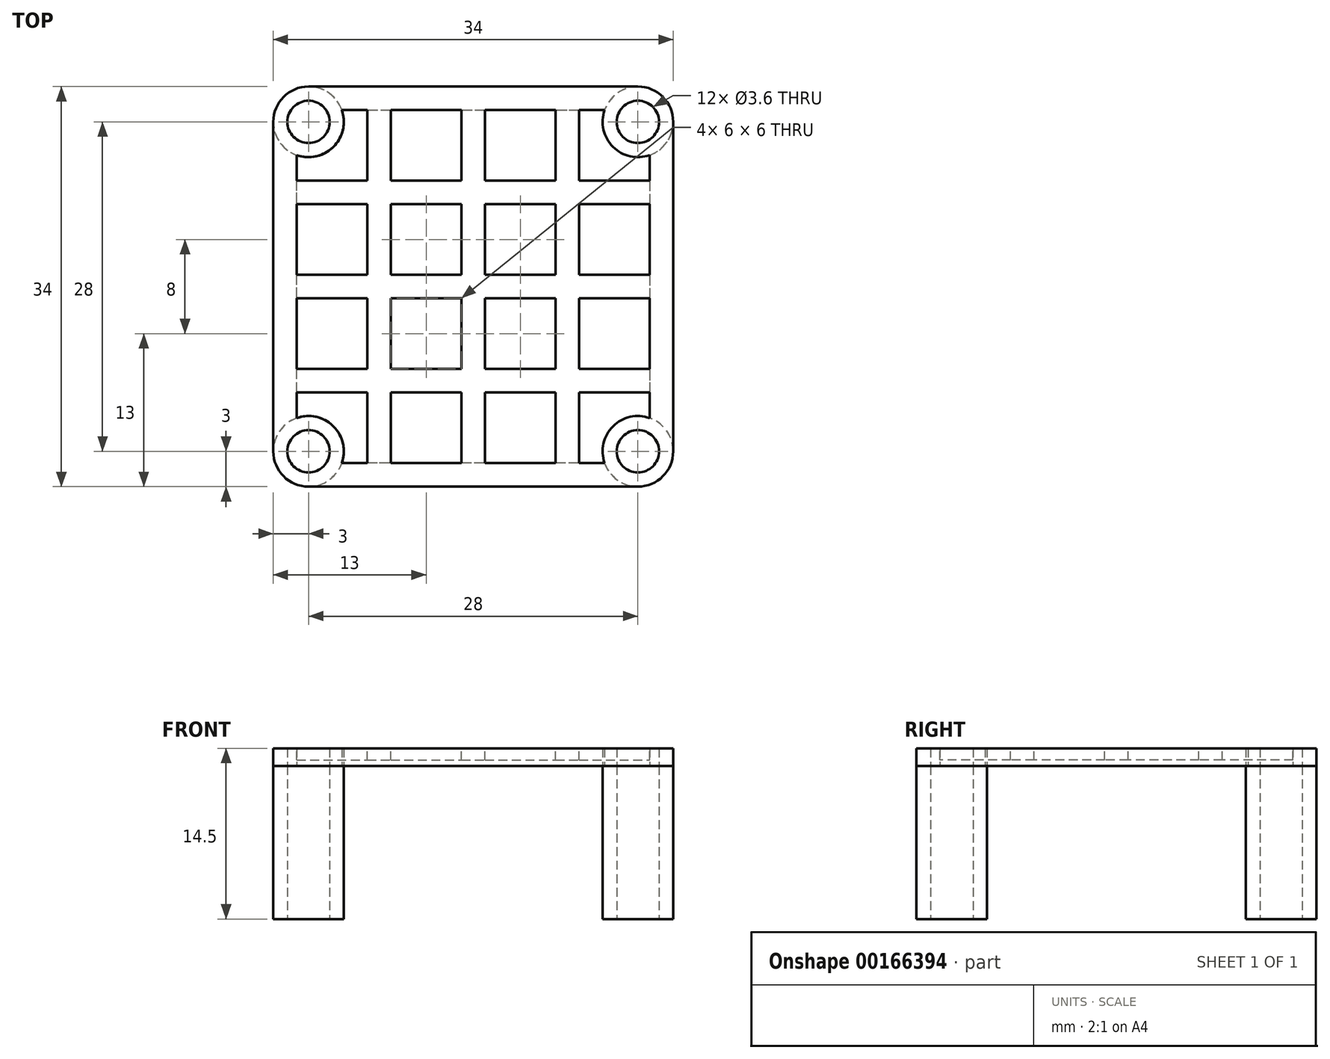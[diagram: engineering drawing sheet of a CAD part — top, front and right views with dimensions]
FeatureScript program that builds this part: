
annotation { "Feature Type Name" : "Feature", "Feature Type Description" : "" }
export const myFeature = defineFeature(function(context is Context, id is Id, definition is map)
    precondition{}
    {
        {
            var Q0;
            Q0=qCreatedBy(makeId("Top.planeOp"),FACE);
            var sketch = newSketch(context, id + "F0", { "sketchPlane" : qUnion([Q0])});
            skCircle(sketch, "E0", {"center": v(14, 14) * mm, "radius": 1.8 * mm});
            skCircle(sketch, "E1", {"center": v(-14, 14) * mm, "radius": 1.8 * mm});
            skCircle(sketch, "E2", {"center": v(-14, -14) * mm, "radius": 1.8 * mm});
            skCircle(sketch, "E3", {"center": v(14, -14) * mm, "radius": 1.8 * mm});
            skCircle(sketch, "E4", {"center": v(-14, 14) * mm, "radius": 3 * mm});
            skCircle(sketch, "E5", {"center": v(-14, -14) * mm, "radius": 3 * mm});
            skCircle(sketch, "E6", {"center": v(14, -14) * mm, "radius": 3 * mm});
            skCircle(sketch, "E7", {"center": v(14, 14) * mm, "radius": 3 * mm});
            skLineSegment(sketch, "E8", {"start": v(17, 14) * mm, "end": v(17, -14) * mm});
            skSolve(sketch);
        }
        {
            var Q0;
            Q0 = qSketchRegion(id + "F0", true);
            extrude(context, id + "F1", {"entities" : qUnion([Q0]), "depth" : 13 * mm});
        }
        {
            var Q0;
            Q0=makeQuery(id+"F1.opExtrude","CAP_FACE",FACE,{"disambiguationData":[OSD([sQuery(id+"F0.wireOp",EDGE,"E0"),sQuery(id+"F0.wireOp",EDGE,"E1"),sQuery(id+"F0.wireOp",EDGE,"E2"),sQuery(id+"F0.wireOp",EDGE,"E3"),sQuery(id+"F0.wireOp",EDGE,"E4"),sQuery(id+"F0.wireOp",EDGE,"E5"),sQuery(id+"F0.wireOp",EDGE,"E6"),sQuery(id+"F0.wireOp",EDGE,"E7"),sQuery(id+"F0.wireOp",EDGE,"E8"),sQuery(id+"F0.wireOp",EDGE,"9i3S1Yhi-saMO-If9d-kcrl-0AW5lP11ECcG"),sQuery(id+"F0.wireOp",EDGE,"0W7b4J66-iXpZ-pcOm-YQU5-B3qUaQrYBzQB"),sQuery(id+"F0.wireOp",EDGE,"YHf7HNGq-JsbW-y9zw-wNTN-EviQUekIIshC")])],"isStart":false});
            var sketch = newSketch(context, id + "F2", { "sketchPlane" : qUnion([Q0])});
            skArc(sketch, "E9.0", {"start": v(-15, 11.17) * mm, "mid": v(-11.88, 11.88) * mm, "end": v(-11.17, 15) * mm});
            skCircle(sketch, "E9.1", {"center": v(-14, 14) * mm, "radius": 1.8 * mm});
            skArc(sketch, "E9.2", {"start": v(11.17, 15) * mm, "mid": v(11.88, 11.88) * mm, "end": v(15, 11.17) * mm});
            skCircle(sketch, "E9.3", {"center": v(14, 14) * mm, "radius": 1.8 * mm});
            skArc(sketch, "E9.4", {"start": v(15, -11.17) * mm, "mid": v(11.88, -11.88) * mm, "end": v(11.17, -15) * mm});
            skCircle(sketch, "E9.5", {"center": v(14, -14) * mm, "radius": 1.8 * mm});
            skCircle(sketch, "E9.6", {"center": v(-14, -14) * mm, "radius": 1.8 * mm});
            skArc(sketch, "E9.7", {"start": v(-11.17, -15) * mm, "mid": v(-11.88, -11.88) * mm, "end": v(-15, -11.17) * mm});
            skLineSegment(sketch, "E10", {"start": v(-14, 17) * mm, "end": v(14, 17) * mm});
            skLineSegment(sketch, "E11", {"start": v(17, 14) * mm, "end": v(17, -14) * mm});
            skLineSegment(sketch, "E12", {"start": v(14, -17) * mm, "end": v(-14, -17) * mm});
            skLineSegment(sketch, "E13", {"start": v(-17, -14) * mm, "end": v(-17, 14) * mm});
            skLineSegment(sketch, "E14.0", {"start": v(-15, -11.17) * mm, "end": v(-15, 11.17) * mm});
            skLineSegment(sketch, "E15.trimOffspring", {"start": v(-11.17, 15) * mm, "end": v(11.17, 15) * mm});
            skArc(sketch, "E16.trimOffspring", {"start": v(-14, 17) * mm, "mid": v(-16.12, 16.12) * mm, "end": v(-17, 14) * mm});
            skArc(sketch, "E17.trimOffspring", {"start": v(17, 14) * mm, "mid": v(16.12, 16.12) * mm, "end": v(14, 17) * mm});
            skLineSegment(sketch, "E18.trimOffspring", {"start": v(15, 11.17) * mm, "end": v(15, -11.17) * mm});
            skLineSegment(sketch, "E19.trimOffspring", {"start": v(11.17, -15) * mm, "end": v(-11.17, -15) * mm});
            skArc(sketch, "E20.trimOffspring", {"start": v(14, -17) * mm, "mid": v(16.12, -16.12) * mm, "end": v(17, -14) * mm});
            skArc(sketch, "E21.trimOffspring", {"start": v(-17, -14) * mm, "mid": v(-16.12, -16.12) * mm, "end": v(-14, -17) * mm});
            skSolve(sketch);
        }
        {
            var Q0;
            Q0 = qSketchRegion(id + "F2", true);
            extrude(context, id + "F3", {"entities" : qUnion([Q0]), "depth" : 1.5 * mm});
        }
        {
            var Q0;
            Q0=makeQuery(id+"F3.opExtrude","CAP_FACE",FACE,{"disambiguationData":[OSD([sQuery(id+"F2.wireOp",EDGE,"E9.0"),sQuery(id+"F2.wireOp",EDGE,"E9.1"),sQuery(id+"F2.wireOp",EDGE,"E9.2"),sQuery(id+"F2.wireOp",EDGE,"E9.3"),sQuery(id+"F2.wireOp",EDGE,"E9.4"),sQuery(id+"F2.wireOp",EDGE,"E9.5"),sQuery(id+"F2.wireOp",EDGE,"E9.6"),sQuery(id+"F2.wireOp",EDGE,"E9.7"),sQuery(id+"F2.wireOp",EDGE,"E10"),sQuery(id+"F2.wireOp",EDGE,"E11"),sQuery(id+"F2.wireOp",EDGE,"E12"),sQuery(id+"F2.wireOp",EDGE,"E13"),sQuery(id+"F2.wireOp",EDGE,"E14.0"),sQuery(id+"F2.wireOp",EDGE,"E15.trimOffspring"),sQuery(id+"F2.wireOp",EDGE,"E16.trimOffspring"),sQuery(id+"F2.wireOp",EDGE,"E17.trimOffspring"),sQuery(id+"F2.wireOp",EDGE,"E18.trimOffspring"),sQuery(id+"F2.wireOp",EDGE,"E19.trimOffspring"),sQuery(id+"F2.wireOp",EDGE,"E20.trimOffspring"),sQuery(id+"F2.wireOp",EDGE,"E21.trimOffspring")])],"isStart":false});
            var sketch = newSketch(context, id + "F4", { "sketchPlane" : qUnion([Q0])});
            skLineSegment(sketch, "E22.0", {"start": v(-1, 15) * mm, "end": v(-1, 9) * mm});
            skLineSegment(sketch, "E23.0", {"start": v(1, 15) * mm, "end": v(1, 9) * mm});
            skLineSegment(sketch, "E24.0", {"start": v(7, 15) * mm, "end": v(7, 9) * mm});
            skLineSegment(sketch, "E25.0", {"start": v(9, 15) * mm, "end": v(9, 9) * mm});
            skLineSegment(sketch, "E26.0", {"start": v(-7, 15) * mm, "end": v(-7, 9) * mm});
            skLineSegment(sketch, "E27.0", {"start": v(-9, 15) * mm, "end": v(-9, 9) * mm});
            skLineSegment(sketch, "E28.0", {"start": v(-15, -1) * mm, "end": v(-9, -1) * mm});
            skLineSegment(sketch, "E29.0", {"start": v(-15, 1) * mm, "end": v(-9, 1) * mm});
            skLineSegment(sketch, "E30.0", {"start": v(-15, 7) * mm, "end": v(-9, 7) * mm});
            skLineSegment(sketch, "E31.0", {"start": v(-15, 9) * mm, "end": v(-9, 9) * mm});
            skLineSegment(sketch, "E32.0", {"start": v(-15, -7) * mm, "end": v(-9, -7) * mm});
            skLineSegment(sketch, "E33.0", {"start": v(-15, -9) * mm, "end": v(-9, -9) * mm});
            skLineSegment(sketch, "E34.trimOffspring", {"start": v(-7, 9) * mm, "end": v(-1, 9) * mm});
            skLineSegment(sketch, "E35.trimOffspring", {"start": v(-7, 7) * mm, "end": v(-1, 7) * mm});
            skLineSegment(sketch, "E36.trimOffspring", {"start": v(-7, 7) * mm, "end": v(-7, 1) * mm});
            skLineSegment(sketch, "E37.trimOffspring", {"start": v(-9, 7) * mm, "end": v(-9, 1) * mm});
            skLineSegment(sketch, "E38.trimOffspring", {"start": v(-1, 7) * mm, "end": v(-1, 1) * mm});
            skLineSegment(sketch, "E39.trimOffspring", {"start": v(1, 7) * mm, "end": v(1, 1) * mm});
            skLineSegment(sketch, "E40.trimOffspring", {"start": v(7, 7) * mm, "end": v(7, 1) * mm});
            skLineSegment(sketch, "E41.trimOffspring", {"start": v(9, 7) * mm, "end": v(9, 1) * mm});
            skLineSegment(sketch, "E42.trimOffspring", {"start": v(9, 9) * mm, "end": v(15, 9) * mm});
            skLineSegment(sketch, "E43.trimOffspring", {"start": v(9, 7) * mm, "end": v(15, 7) * mm});
            skLineSegment(sketch, "E44.trimOffspring", {"start": v(1, 7) * mm, "end": v(7, 7) * mm});
            skLineSegment(sketch, "E45.trimOffspring", {"start": v(1, 9) * mm, "end": v(7, 9) * mm});
            skLineSegment(sketch, "E46.trimOffspring", {"start": v(9, 1) * mm, "end": v(15, 1) * mm});
            skLineSegment(sketch, "E47.trimOffspring", {"start": v(9, -1) * mm, "end": v(15, -1) * mm});
            skLineSegment(sketch, "E48.trimOffspring", {"start": v(9, -7) * mm, "end": v(15, -7) * mm});
            skLineSegment(sketch, "E49.trimOffspring", {"start": v(9, -9) * mm, "end": v(15, -9) * mm});
            skLineSegment(sketch, "E50.trimOffspring", {"start": v(9, -9) * mm, "end": v(9, -15) * mm});
            skLineSegment(sketch, "E51.trimOffspring", {"start": v(7, -9) * mm, "end": v(7, -15) * mm});
            skLineSegment(sketch, "E52.trimOffspring", {"start": v(9, -1) * mm, "end": v(9, -7) * mm});
            skLineSegment(sketch, "E53.trimOffspring", {"start": v(7, -1) * mm, "end": v(7, -7) * mm});
            skLineSegment(sketch, "E54.trimOffspring", {"start": v(1, -9) * mm, "end": v(1, -15) * mm});
            skLineSegment(sketch, "E55.trimOffspring", {"start": v(1, -7) * mm, "end": v(7, -7) * mm});
            skLineSegment(sketch, "E56.trimOffspring", {"start": v(1, -9) * mm, "end": v(7, -9) * mm});
            skLineSegment(sketch, "E57.trimOffspring", {"start": v(-1, -9) * mm, "end": v(-1, -15) * mm});
            skLineSegment(sketch, "E58.trimOffspring", {"start": v(-7, -9) * mm, "end": v(-7, -15) * mm});
            skLineSegment(sketch, "E59.trimOffspring", {"start": v(-7, -7) * mm, "end": v(-1, -7) * mm});
            skLineSegment(sketch, "E60.trimOffspring", {"start": v(-7, -9) * mm, "end": v(-1, -9) * mm});
            skLineSegment(sketch, "E61.trimOffspring", {"start": v(-9, -9) * mm, "end": v(-9, -15) * mm});
            skLineSegment(sketch, "E62.trimOffspring", {"start": v(-7, -1) * mm, "end": v(-1, -1) * mm});
            skLineSegment(sketch, "E63.trimOffspring", {"start": v(-7, -1) * mm, "end": v(-7, -7) * mm});
            skLineSegment(sketch, "E64.trimOffspring", {"start": v(-9, -1) * mm, "end": v(-9, -7) * mm});
            skLineSegment(sketch, "E65.trimOffspring", {"start": v(-7, 1) * mm, "end": v(-1, 1) * mm});
            skLineSegment(sketch, "E66.trimOffspring", {"start": v(1, 1) * mm, "end": v(7, 1) * mm});
            skLineSegment(sketch, "E67.trimOffspring", {"start": v(1, -1) * mm, "end": v(7, -1) * mm});
            skLineSegment(sketch, "E68.trimOffspring", {"start": v(1, -1) * mm, "end": v(1, -7) * mm});
            skLineSegment(sketch, "E69.trimOffspring", {"start": v(-1, -1) * mm, "end": v(-1, -7) * mm});
            skSolve(sketch);
        }
        {
            var Q0;
            {var subQ24=sQuery(id+"F4.wireOp",EDGE,"E22.0");Q0=makeQuery(id+"F4.imprint","IMPRINT",FACE,{"disambiguationData":[TD([[makeQuery(id+"F4.imprint","IMPRINT",EDGE,{"derivedFrom":subQ24}),1.0]])]});}
            extrude(context, id + "F5", {"entities" : qUnion([Q0]), "operationType" : NewBodyOperationType.ADD, "oppositeDirection" : true, "depth" : 1 * mm});
        }
    });
